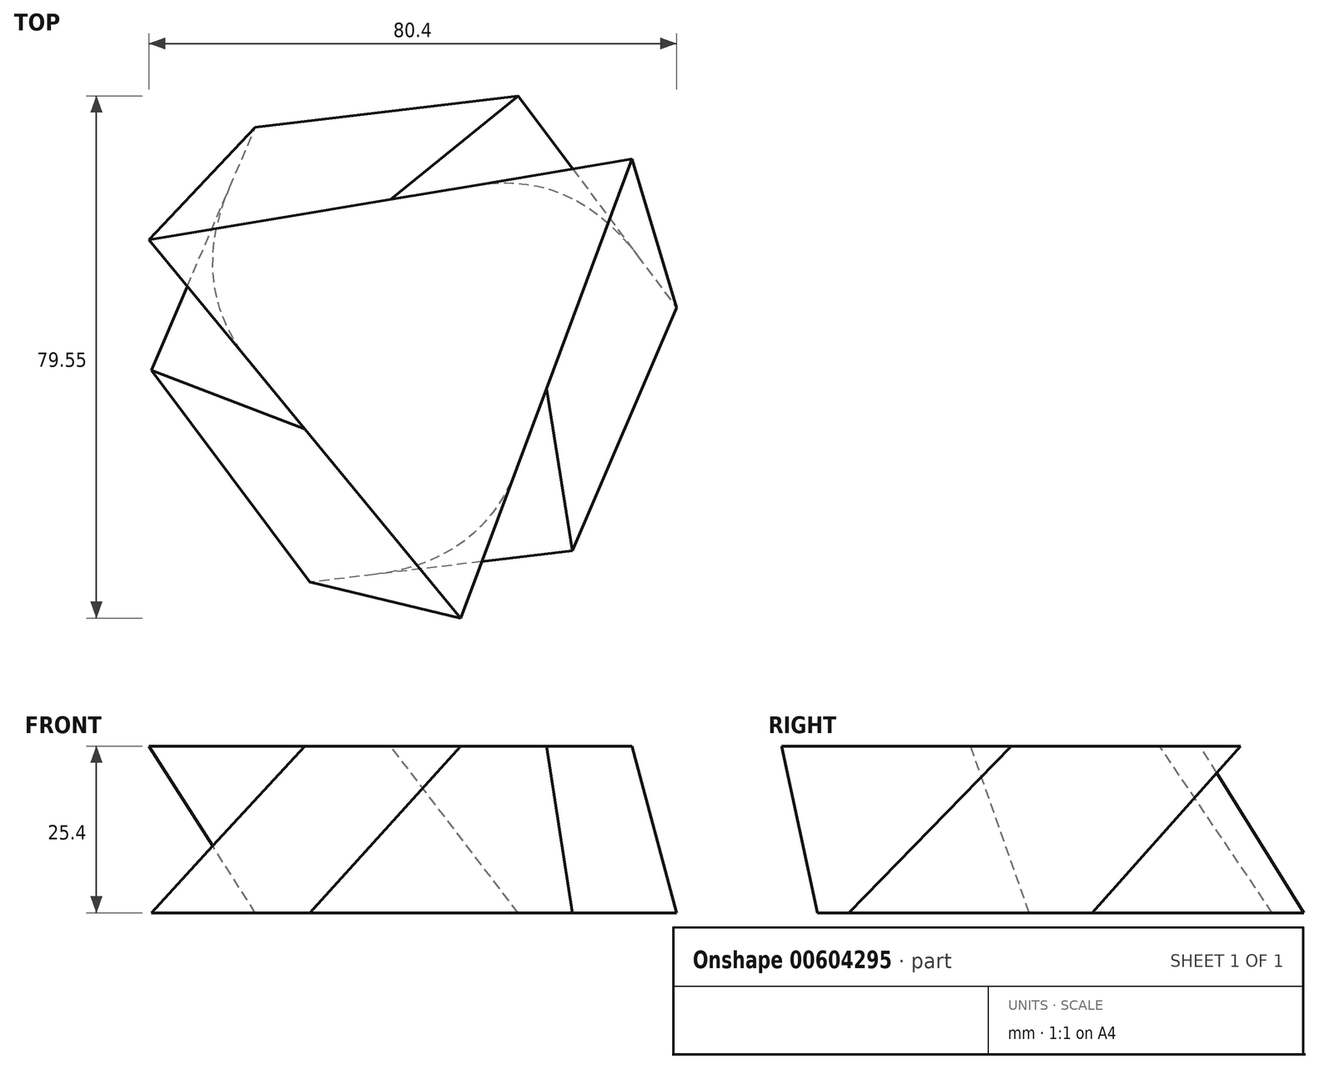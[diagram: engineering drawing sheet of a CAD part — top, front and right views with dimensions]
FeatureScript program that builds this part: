
annotation { "Feature Type Name" : "Feature", "Feature Type Description" : "" }
export const myFeature = defineFeature(function(context is Context, id is Id, definition is map)
    precondition{}
    {
        {
            var Q0;
            Q0=qCreatedBy(makeId("Top.planeOp"),FACE);
            cPlane(context, id + "F0", {"entities" : qUnion([Q0]), "cplaneType" : CPlaneType.OFFSET, "offset" : 25.4 * mm, "width" : 152.4 * mm, "height" : 152.4 * mm});
        }
        {
            var Q0;
            Q0=qCreatedBy(makeId("Top.planeOp"),FACE);
            var sketch = newSketch(context, id + "F1", { "sketchPlane" : qUnion([Q0])});
            skCircle(sketch, "E0.cCircle", {"center": v(0, 0) * mm, "radius": 34.9 * mm, "construction": true});
            skLineSegment(sketch, "E0.0", {"start": v(-15.87, -37.04) * mm, "end": v(-40.02, -4.78) * mm});
            skLineSegment(sketch, "E0.1", {"start": v(-40.02, -4.78) * mm, "end": v(-24.15, 32.26) * mm});
            skLineSegment(sketch, "E0.2", {"start": v(-24.15, 32.26) * mm, "end": v(15.87, 37.04) * mm});
            skLineSegment(sketch, "E0.3", {"start": v(15.87, 37.04) * mm, "end": v(40.02, 4.78) * mm});
            skLineSegment(sketch, "E0.4", {"start": v(40.02, 4.78) * mm, "end": v(24.15, -32.26) * mm});
            skLineSegment(sketch, "E0.5", {"start": v(24.15, -32.26) * mm, "end": v(-15.87, -37.04) * mm});
            skPoint(sketch, "E0.0.midPoint", {"position": v(-27.94, -20.91) * mm});
            skSolve(sketch);
        }
        {
            var Q0;
            Q0=qCreatedBy(id+"F0.planeOp",FACE);
            var sketch = newSketch(context, id + "F2", { "sketchPlane" : qUnion([Q0])});
            skCircle(sketch, "E1.cCircle", {"center": v(0, 0) * mm, "radius": 21.55 * mm, "construction": true});
            skLineSegment(sketch, "E1.0", {"start": v(7.12, -42.51) * mm, "end": v(-40.38, 15.09) * mm});
            skLineSegment(sketch, "E1.1", {"start": v(-40.38, 15.09) * mm, "end": v(33.26, 27.42) * mm});
            skLineSegment(sketch, "E1.2", {"start": v(33.26, 27.42) * mm, "end": v(7.12, -42.51) * mm});
            skPoint(sketch, "E1.0.midPoint", {"position": v(-16.63, -13.71) * mm});
            skSolve(sketch);
        }
        {
            var Q0;
            Q0=makeQuery(id+"F1.imprint","IMPRINT",FACE,{"disambiguationData":[TD([[makeQuery(id+"F1.imprint","IMPRINT",EDGE,{"derivedFrom":sQuery(id+"F1.wireOp",EDGE,"E0.0")}),-1.0]])]});
            var Q1;
            Q1 = qSketchRegion(id + "F2", true);
            loft(context, id + "F3", {"sheetProfilesArray" : [{ "sheetProfileEntities" : qUnion([Q0]) }, { "sheetProfileEntities" : qUnion([Q1]) }]});
        }
    });
